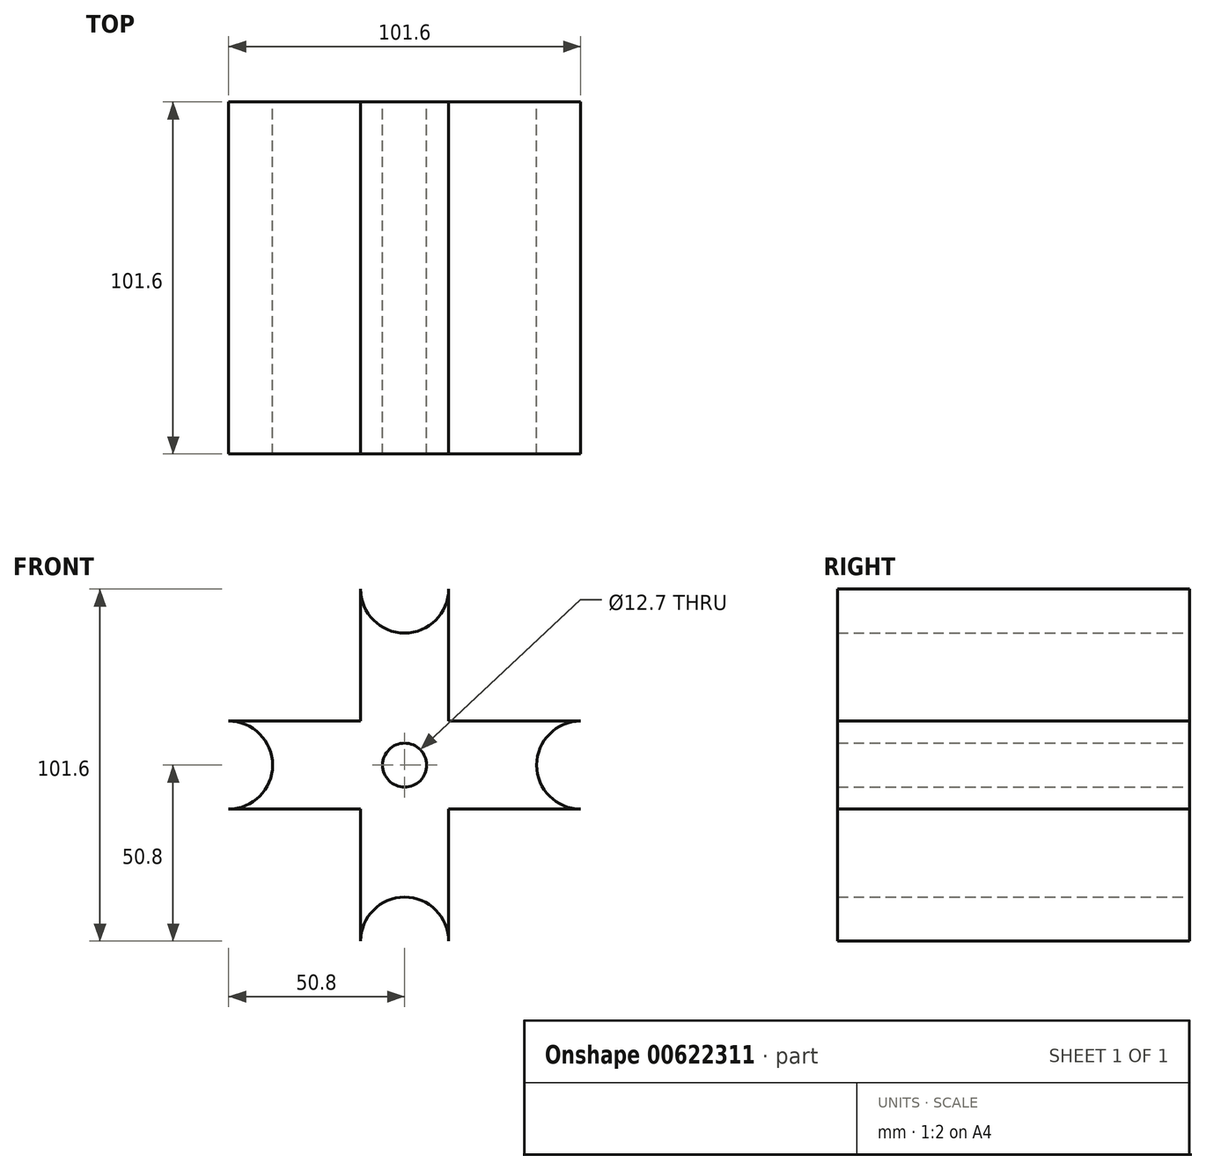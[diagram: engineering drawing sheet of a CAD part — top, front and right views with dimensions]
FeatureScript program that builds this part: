
annotation { "Feature Type Name" : "Feature", "Feature Type Description" : "" }
export const myFeature = defineFeature(function(context is Context, id is Id, definition is map)
    precondition{}
    {
        {
            var Q0;
            Q0=qCreatedBy(makeId("Front.planeOp"),FACE);
            var sketch = newSketch(context, id + "F0", { "sketchPlane" : qUnion([Q0])});
            skLineSegment(sketch, "E0", {"start": v(-12.7, 12.7) * mm, "end": v(-12.7, 50.8) * mm});
            skLineSegment(sketch, "E1", {"start": v(-12.7, 12.7) * mm, "end": v(-50.8, 12.7) * mm});
            skLineSegment(sketch, "E2", {"start": v(-12.7, 50.8) * mm, "end": v(12.7, 50.8) * mm, "construction": true});
            skLineSegment(sketch, "E3", {"start": v(12.7, 50.8) * mm, "end": v(12.7, 12.7) * mm});
            skLineSegment(sketch, "E4", {"start": v(12.7, 12.7) * mm, "end": v(50.8, 12.7) * mm});
            skArc(sketch, "E5", {"start": v(-12.7, 50.8) * mm, "mid": v(0, 38.1) * mm, "end": v(12.7, 50.8) * mm});
            skLineSegment(sketch, "E6.MirrorCS", {"start": v(-12.7, -12.7) * mm, "end": v(-50.8, -12.7) * mm});
            skLineSegment(sketch, "E7.MirrorCS", {"start": v(-12.7, -12.7) * mm, "end": v(-12.7, -50.8) * mm});
            skArc(sketch, "E8.MirrorCS", {"start": v(-12.7, -50.8) * mm, "mid": v(0, -38.1) * mm, "end": v(12.7, -50.8) * mm});
            skLineSegment(sketch, "E9.MirrorCS", {"start": v(12.7, -50.8) * mm, "end": v(12.7, -12.7) * mm});
            skLineSegment(sketch, "E10.MirrorCS", {"start": v(12.7, -12.7) * mm, "end": v(50.8, -12.7) * mm});
            skArc(sketch, "E11", {"start": v(-50.8, -12.7) * mm, "mid": v(-38.1, 0) * mm, "end": v(-50.8, 12.7) * mm});
            skArc(sketch, "E12", {"start": v(50.8, 12.7) * mm, "mid": v(38.1, 0) * mm, "end": v(50.8, -12.7) * mm});
            skCircle(sketch, "E13", {"center": v(0, 0) * mm, "radius": 6.35 * mm});
            skSolve(sketch);
        }
        {
            var Q0;
            Q0=makeQuery(id+"F0.imprint","IMPRINT",FACE,{"disambiguationData":[TD([[makeQuery(id+"F0.imprint","IMPRINT",EDGE,{"derivedFrom":sQuery(id+"F0.wireOp",EDGE,"E0")}),-1.0]])]});
            extrude(context, id + "F1", {"entities" : qUnion([Q0]), "depth" : 101.6 * mm, "offsetDistance" : 25.4 * mm});
        }
    });
